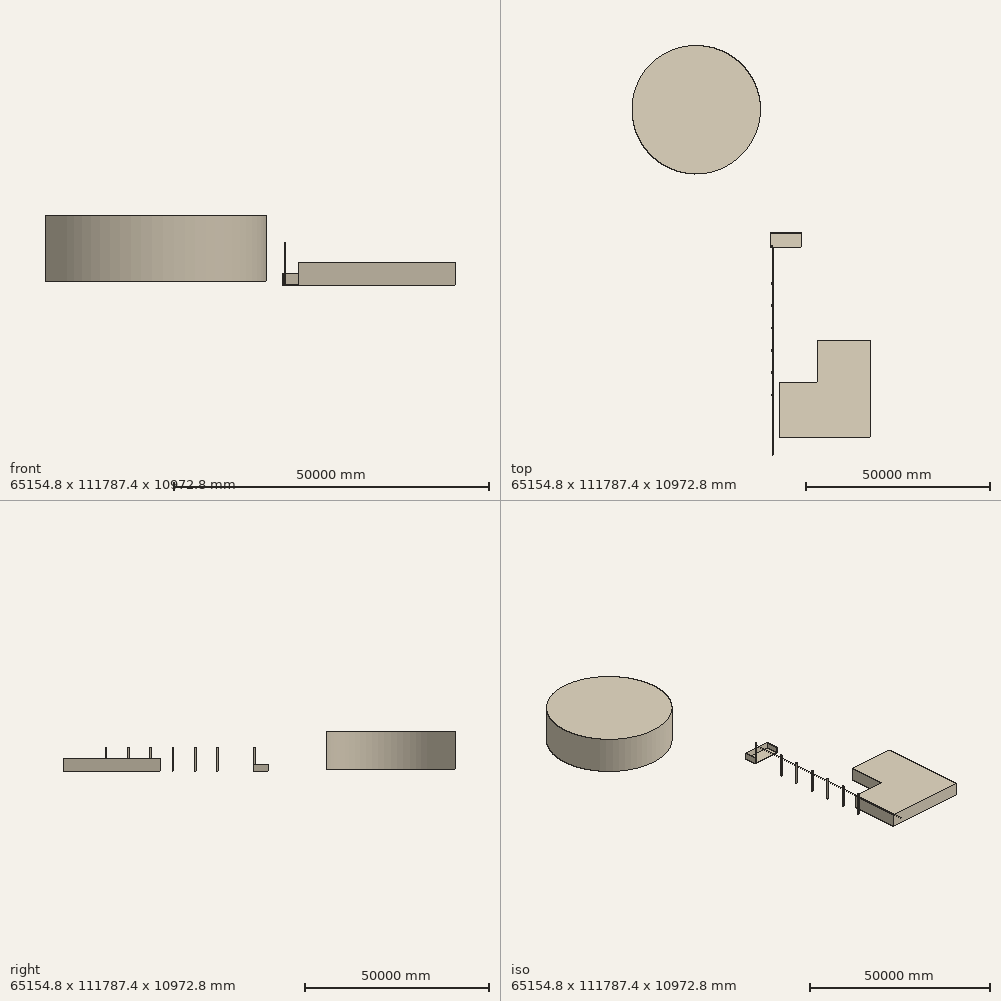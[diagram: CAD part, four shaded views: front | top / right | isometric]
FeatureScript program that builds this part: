
annotation { "Feature Type Name" : "Feature", "Feature Type Description" : "" }
export const myFeature = defineFeature(function(context is Context, id is Id, definition is map)
    precondition{}
    {
        {
            var Q0;
            Q0=qCreatedBy(makeId("Top.planeOp"),FACE);
            cPlane(context, id + "F0", {"entities" : qUnion([Q0]), "cplaneType" : CPlaneType.OFFSET, "offset" : 609.6 * mm, "width" : 152.4 * mm, "height" : 152.4 * mm});
        }
        {
            var Q0;
            Q0=qCreatedBy(makeId("Top.planeOp"),FACE);
            cPlane(context, id + "F1", {"entities" : qUnion([Q0]), "cplaneType" : CPlaneType.OFFSET, "offset" : 5486.4 * mm, "width" : 152.4 * mm, "height" : 152.4 * mm});
        }
        {
            var Q0;
            Q0=qCreatedBy(makeId("Top.planeOp"),FACE);
            var sketch = newSketch(context, id + "F2", { "sketchPlane" : qUnion([Q0])});
            skLineSegment(sketch, "E0.bottom", {"start": v(91832.86, -48932.37) * mm, "end": v(100367.26, -48932.37) * mm});
            skLineSegment(sketch, "E0.top", {"start": v(91832.86, -52894.77) * mm, "end": v(100367.26, -52894.77) * mm});
            skLineSegment(sketch, "E0.left", {"start": v(91832.86, -48932.37) * mm, "end": v(91832.86, -52894.77) * mm});
            skLineSegment(sketch, "E0.right", {"start": v(100367.26, -48932.37) * mm, "end": v(100367.26, -52894.77) * mm});
            skSolve(sketch);
        }
        {
            var Q0;
            Q0=qCreatedBy(id+"F0.planeOp",FACE);
            var sketch = newSketch(context, id + "F3", { "sketchPlane" : qUnion([Q0])});
            skCircle(sketch, "E1", {"center": v(71615.6, -15371.14) * mm, "radius": 17526 * mm});
            skCircle(sketch, "E2", {"center": v(107429.18, -15472.76) * mm, "radius": 12192 * mm, "construction": true});
            skLineSegment(sketch, "E3", {"start": v(89141.6, -15371.14) * mm, "end": v(95237.6, -15371.14) * mm, "construction": true});
            skLineSegment(sketch, "E4", {"start": v(92750.37, -15371.14) * mm, "end": v(92750.37, -48945.01) * mm, "construction": true});
            skLineSegment(sketch, "E5", {"start": v(89141.6, -15371.14) * mm, "end": v(92750.37, -15371.14) * mm});
            skLineSegment(sketch, "E6", {"start": v(92750.37, -48945.01) * mm, "end": v(92750.37, -15371.14) * mm});
            skLineSegment(sketch, "E7", {"start": v(92750.37, -15371.14) * mm, "end": v(92750.37, 1596.04) * mm, "construction": true});
            skLineSegment(sketch, "E8", {"start": v(72228.34, -32886.43) * mm, "end": v(72228.34, -36341.72) * mm});
            skLineSegment(sketch, "E9", {"start": v(72228.34, -36341.72) * mm, "end": v(92750.37, -36341.72) * mm});
            skLineSegment(sketch, "E10", {"start": v(92750.37, -52872.68) * mm, "end": v(92750.37, -109645.42) * mm});
            skLineSegment(sketch, "E11", {"start": v(92750.37, -109645.42) * mm, "end": v(183269.45, -109645.42) * mm});
            skLineSegment(sketch, "E12", {"start": v(92750.37, -109645.42) * mm, "end": v(33186.4, -109645.42) * mm});
            skLineSegment(sketch, "E13", {"start": v(183269.45, -109645.42) * mm, "end": v(183269.45, -122414.02) * mm});
            skLineSegment(sketch, "E14", {"start": v(94104.32, -27367.16) * mm, "end": v(94104.32, -108353.84) * mm});
            skLineSegment(sketch, "E15", {"start": v(94104.32, -108353.84) * mm, "end": v(184651.92, -108353.84) * mm});
            skLineSegment(sketch, "E16", {"start": v(94104.32, -108353.84) * mm, "end": v(31662.4, -108353.84) * mm});
            skLineSegment(sketch, "E17", {"start": v(184651.92, -108353.84) * mm, "end": v(184651.92, -120890.02) * mm});
            skSolve(sketch);
        }
        {
            var Q0;
            Q0=qCreatedBy(makeId("Top.planeOp"),FACE);
            var sketch = newSketch(context, id + "F4", { "sketchPlane" : qUnion([Q0])});
            skLineSegment(sketch, "E18.bottom", {"start": v(92083.2, -52401.42) * mm, "end": v(92311.8, -52401.42) * mm});
            skLineSegment(sketch, "E18.top", {"start": v(92083.2, -52858.62) * mm, "end": v(92311.8, -52858.62) * mm});
            skLineSegment(sketch, "E18.left", {"start": v(92083.2, -52401.42) * mm, "end": v(92083.2, -52858.62) * mm});
            skLineSegment(sketch, "E18.right", {"start": v(92311.8, -52401.42) * mm, "end": v(92311.8, -52858.62) * mm});
            skLineSegment(sketch, "E19", {"start": v(92311.8, -52858.62) * mm, "end": v(92311.8, -109632.54) * mm, "construction": true});
            skLineSegment(sketch, "E20.0", {"start": v(92464.2, -52858.62) * mm, "end": v(92464.2, -109632.54) * mm});
            skSolve(sketch);
        }
        {
            var Q0;
            Q0=qCreatedBy(makeId("Top.planeOp"),FACE);
            var sketch = newSketch(context, id + "F5", { "sketchPlane" : qUnion([Q0])});
            skLineSegment(sketch, "E21.bottom", {"start": v(92083.2, -62459.82) * mm, "end": v(92311.8, -62459.82) * mm});
            skLineSegment(sketch, "E21.top", {"start": v(92083.2, -62917.02) * mm, "end": v(92311.8, -62917.02) * mm});
            skLineSegment(sketch, "E21.left", {"start": v(92083.2, -62459.82) * mm, "end": v(92083.2, -62917.02) * mm});
            skLineSegment(sketch, "E21.right", {"start": v(92311.8, -62459.82) * mm, "end": v(92311.8, -62917.02) * mm});
            skLineSegment(sketch, "E22.0", {"start": v(92311.8, -52858.62) * mm, "end": v(92311.8, -109632.54) * mm, "construction": true});
            skLineSegment(sketch, "E23.bottom", {"start": v(92083.2, -68555.82) * mm, "end": v(92311.8, -68555.82) * mm});
            skLineSegment(sketch, "E23.top", {"start": v(92083.2, -69013.02) * mm, "end": v(92311.8, -69013.02) * mm});
            skLineSegment(sketch, "E23.left", {"start": v(92083.2, -68555.82) * mm, "end": v(92083.2, -69013.02) * mm});
            skLineSegment(sketch, "E23.right", {"start": v(92311.8, -68555.82) * mm, "end": v(92311.8, -69013.02) * mm});
            skLineSegment(sketch, "E24.bottom", {"start": v(92083.2, -74651.82) * mm, "end": v(92311.8, -74651.82) * mm});
            skLineSegment(sketch, "E24.top", {"start": v(92083.2, -75109.02) * mm, "end": v(92311.8, -75109.02) * mm});
            skLineSegment(sketch, "E24.left", {"start": v(92083.2, -74651.82) * mm, "end": v(92083.2, -75109.02) * mm});
            skLineSegment(sketch, "E24.right", {"start": v(92311.8, -74651.82) * mm, "end": v(92311.8, -75109.02) * mm});
            skLineSegment(sketch, "E25.bottom", {"start": v(92083.2, -80747.82) * mm, "end": v(92311.8, -80747.82) * mm});
            skLineSegment(sketch, "E25.top", {"start": v(92083.2, -81205.02) * mm, "end": v(92311.8, -81205.02) * mm});
            skLineSegment(sketch, "E25.left", {"start": v(92083.2, -80747.82) * mm, "end": v(92083.2, -81205.02) * mm});
            skLineSegment(sketch, "E25.right", {"start": v(92311.8, -80747.82) * mm, "end": v(92311.8, -81205.02) * mm});
            skLineSegment(sketch, "E26.bottom", {"start": v(92083.2, -86843.82) * mm, "end": v(92311.8, -86843.82) * mm});
            skLineSegment(sketch, "E26.top", {"start": v(92083.2, -87301.02) * mm, "end": v(92311.8, -87301.02) * mm});
            skLineSegment(sketch, "E26.left", {"start": v(92083.2, -86843.82) * mm, "end": v(92083.2, -87301.02) * mm});
            skLineSegment(sketch, "E26.right", {"start": v(92311.8, -86843.82) * mm, "end": v(92311.8, -87301.02) * mm});
            skLineSegment(sketch, "E27.bottom", {"start": v(92083.2, -92939.82) * mm, "end": v(92311.8, -92939.82) * mm});
            skLineSegment(sketch, "E27.top", {"start": v(92083.2, -93397.02) * mm, "end": v(92311.8, -93397.02) * mm});
            skLineSegment(sketch, "E27.left", {"start": v(92083.2, -92939.82) * mm, "end": v(92083.2, -93397.02) * mm});
            skLineSegment(sketch, "E27.right", {"start": v(92311.8, -92939.82) * mm, "end": v(92311.8, -93397.02) * mm});
            skSolve(sketch);
        }
        {
            var Q0;
            Q0=makeQuery(id+"F2.imprint","IMPRINT",FACE,{"disambiguationData":[TD([[makeQuery(id+"F2.imprint","IMPRINT",EDGE,{"derivedFrom":sQuery(id+"F2.wireOp",EDGE,"E0.bottom")}),-1.0]])]});
            extrude(context, id + "F6", {"entities" : qUnion([Q0]), "depth" : 1828.8 * mm});
        }
        {
            var Q0;
            Q0=makeQuery(id+"F6.opExtrude","CAP_FACE",FACE,{"disambiguationData":[OSD([sQuery(id+"F2.wireOp",EDGE,"E0.bottom"),sQuery(id+"F2.wireOp",EDGE,"E0.top"),sQuery(id+"F2.wireOp",EDGE,"E0.left"),sQuery(id+"F2.wireOp",EDGE,"E0.right")])],"isStart":false});
            var Q1;
            Q1=makeQuery(id+"F6.opExtrude","SWEPT_FACE",FACE,{"disambiguationData":[OSD([sQuery(id+"F2.wireOp",EDGE,"E0.top")])]});
            shell(context, id + "F7", {"entities" : qUnion([Q0, Q1]), "thickness" : 152.4 * mm});
        }
        {
            var Q0;
            {var subQ0=sQuery(id+"F3.wireOp",EDGE,"E1");var subQ1=makeQuery(id+"F3.imprint","INTERSECT",VERTEX,{"derivedFrom":[subQ0,sQuery(id+"F3.wireOp",EDGE,"E5")]});Q0=makeQuery(id+"F3.imprint","IMPRINT",FACE,{"disambiguationData":[TD([[makeQuery(id+"F3.imprint","IMPRINT",EDGE,{"disambiguationData":[TD([[subQ1,-1.0]])],"derivedFrom":subQ0}),1.0]])]});}
            extrude(context, id + "F8", {"entities" : qUnion([Q0]), "depth" : 10363.2 * mm});
        }
        {
            var Q0;
            Q0=qCreatedBy(makeId("Top.planeOp"),FACE);
            var sketch = newSketch(context, id + "F9", { "sketchPlane" : qUnion([Q0])});
            skLineSegment(sketch, "E28", {"start": v(119244.38, -78213.5) * mm, "end": v(119244.38, -104714.61) * mm});
            skLineSegment(sketch, "E29", {"start": v(119244.38, -104714.61) * mm, "end": v(94322.8, -104714.61) * mm});
            skLineSegment(sketch, "E30", {"start": v(94322.8, -104714.61) * mm, "end": v(94322.8, -89796.77) * mm});
            skLineSegment(sketch, "E31", {"start": v(94322.8, -89796.77) * mm, "end": v(104677.54, -89796.77) * mm});
            skLineSegment(sketch, "E32", {"start": v(104677.54, -89796.77) * mm, "end": v(104677.54, -78213.5) * mm});
            skLineSegment(sketch, "E33", {"start": v(104677.54, -78213.5) * mm, "end": v(119244.38, -78213.5) * mm});
            skSolve(sketch);
        }
        {
            var Q0;
            Q0 = qSketchRegion(id + "F9", true);
            extrude(context, id + "F10", {"entities" : qUnion([Q0]), "depth" : 3657.6 * mm});
        }
        {
            var Q0;
            Q0=makeQuery(id+"F4.imprint","IMPRINT",FACE,{"disambiguationData":[TD([[makeQuery(id+"F4.imprint","IMPRINT",EDGE,{"derivedFrom":sQuery(id+"F4.wireOp",EDGE,"E18.bottom")}),-1.0]])]});
            extrude(context, id + "F11", {"entities" : qUnion([Q0]), "depth" : 6705.6 * mm});
        }
        {
            var Q0;
            Q0=makeQuery(id+"F5.imprint","IMPRINT",FACE,{"disambiguationData":[TD([[makeQuery(id+"F5.imprint","IMPRINT",EDGE,{"derivedFrom":sQuery(id+"F5.wireOp",EDGE,"E21.bottom")}),-1.0]])]});
            var Q1;
            Q1=makeQuery(id+"F5.imprint","IMPRINT",FACE,{"disambiguationData":[TD([[makeQuery(id+"F5.imprint","IMPRINT",EDGE,{"derivedFrom":sQuery(id+"F5.wireOp",EDGE,"E23.bottom")}),-1.0]])]});
            var Q2;
            Q2=makeQuery(id+"F5.imprint","IMPRINT",FACE,{"disambiguationData":[TD([[makeQuery(id+"F5.imprint","IMPRINT",EDGE,{"derivedFrom":sQuery(id+"F5.wireOp",EDGE,"E24.bottom")}),-1.0]])]});
            var Q3;
            Q3=makeQuery(id+"F5.imprint","IMPRINT",FACE,{"disambiguationData":[TD([[makeQuery(id+"F5.imprint","IMPRINT",EDGE,{"derivedFrom":sQuery(id+"F5.wireOp",EDGE,"E25.bottom")}),-1.0]])]});
            var Q4;
            Q4=makeQuery(id+"F5.imprint","IMPRINT",FACE,{"disambiguationData":[TD([[makeQuery(id+"F5.imprint","IMPRINT",EDGE,{"derivedFrom":sQuery(id+"F5.wireOp",EDGE,"E26.bottom")}),-1.0]])]});
            var Q5;
            Q5=makeQuery(id+"F5.imprint","IMPRINT",FACE,{"disambiguationData":[TD([[makeQuery(id+"F5.imprint","IMPRINT",EDGE,{"derivedFrom":sQuery(id+"F5.wireOp",EDGE,"E27.bottom")}),-1.0]])]});
            var Q6;
            Q6=sQuery(id+"F5.wireOp",EDGE,"E27.bottom");
            var Q7;
            Q7=sQuery(id+"F5.wireOp",EDGE,"E26.right");
            var Q8;
            Q8=sQuery(id+"F5.wireOp",EDGE,"E23.right");
            var Q9;
            Q9=sQuery(id+"F5.wireOp",EDGE,"E27.left");
            var Q10;
            Q10=sQuery(id+"F5.wireOp",EDGE,"E24.bottom");
            var Q11;
            Q11=sQuery(id+"F5.wireOp",EDGE,"E21.top");
            var Q12;
            Q12=sQuery(id+"F5.wireOp",EDGE,"E25.bottom");
            var Q13;
            Q13=sQuery(id+"F5.wireOp",EDGE,"E24.right");
            var Q14;
            Q14=sQuery(id+"F5.wireOp",EDGE,"E27.right");
            var Q15;
            Q15=sQuery(id+"F5.wireOp",EDGE,"E25.right");
            var Q16;
            Q16=sQuery(id+"F5.wireOp",EDGE,"E21.right");
            var Q17;
            Q17=sQuery(id+"F5.wireOp",EDGE,"E26.left");
            var Q18;
            Q18=sQuery(id+"F5.wireOp",EDGE,"E23.top");
            var Q19;
            Q19=sQuery(id+"F5.wireOp",EDGE,"E25.left");
            var Q20;
            Q20=sQuery(id+"F5.wireOp",EDGE,"E21.left");
            var Q21;
            Q21=sQuery(id+"F5.wireOp",EDGE,"E26.bottom");
            var Q22;
            Q22=sQuery(id+"F5.wireOp",EDGE,"E26.top");
            var Q23;
            Q23=sQuery(id+"F5.wireOp",EDGE,"E25.top");
            var Q24;
            Q24=sQuery(id+"F5.wireOp",EDGE,"E23.left");
            var Q25;
            Q25=sQuery(id+"F5.wireOp",EDGE,"E24.left");
            var Q26;
            Q26=sQuery(id+"F5.wireOp",EDGE,"E27.top");
            var Q27;
            Q27=sQuery(id+"F5.wireOp",EDGE,"E21.bottom");
            var Q28;
            Q28=sQuery(id+"F5.wireOp",EDGE,"E23.bottom");
            var Q29;
            Q29=sQuery(id+"F5.wireOp",EDGE,"E24.top");
            extrude(context, id + "F12", {"entities" : qUnion([Q0, Q1, Q2, Q3, Q4, Q5]), "surfaceEntities" : qUnion([Q6, Q7, Q8, Q9, Q10, Q11, Q12, Q13, Q14, Q15, Q16, Q17, Q18, Q19, Q20, Q21, Q22, Q23, Q24, Q25, Q26, Q27, Q28, Q29]), "depth" : 6705.6 * mm});
        }
        {
            var Q0;
            Q0=qCreatedBy(id+"F1.planeOp",FACE);
            var sketch = newSketch(context, id + "F13", { "sketchPlane" : qUnion([Q0])});
            skLineSegment(sketch, "E34.0", {"start": v(92464.2, -52858.62) * mm, "end": v(92464.2, -109632.54) * mm, "construction": true});
            skSolve(sketch);
        }
        {
            var Q0;
            Q0=sQuery(id+"F13.wireOp",VERTEX,"E34.0.start");
            var Q1;
            Q1=sQuery(id+"F13.wireOp",EDGE,"E34.0");
            cPlane(context, id + "F14", {"entities" : qUnion([Q0, Q1]), "cplaneType" : CPlaneType.LINE_POINT, "offset" : 25.4 * mm, "width" : 152.4 * mm, "height" : 152.4 * mm});
        }
        {
            var Q0;
            Q0=qCreatedBy(id+"F14.planeOp",FACE);
            var sketch = newSketch(context, id + "F15", { "sketchPlane" : qUnion([Q0])});
            skCircle(sketch, "E35", {"center": v(92464.2, 5486.4) * mm, "radius": 76.2 * mm});
            skSolve(sketch);
        }
        {
            var Q0;
            Q0=makeQuery(id+"F15.imprint","IMPRINT",FACE,{"disambiguationData":[TD([[makeQuery(id+"F15.imprint","IMPRINT",EDGE,{"derivedFrom":sQuery(id+"F15.wireOp",EDGE,"E35")}),1.0]])]});
            var Q1;
            Q1=sQuery(id+"F4.wireOp",EDGE,"E20.0");
            sweep(context, id + "F16", {"profiles" : qUnion([Q0]), "path" : qUnion([Q1])});
        }
    });
